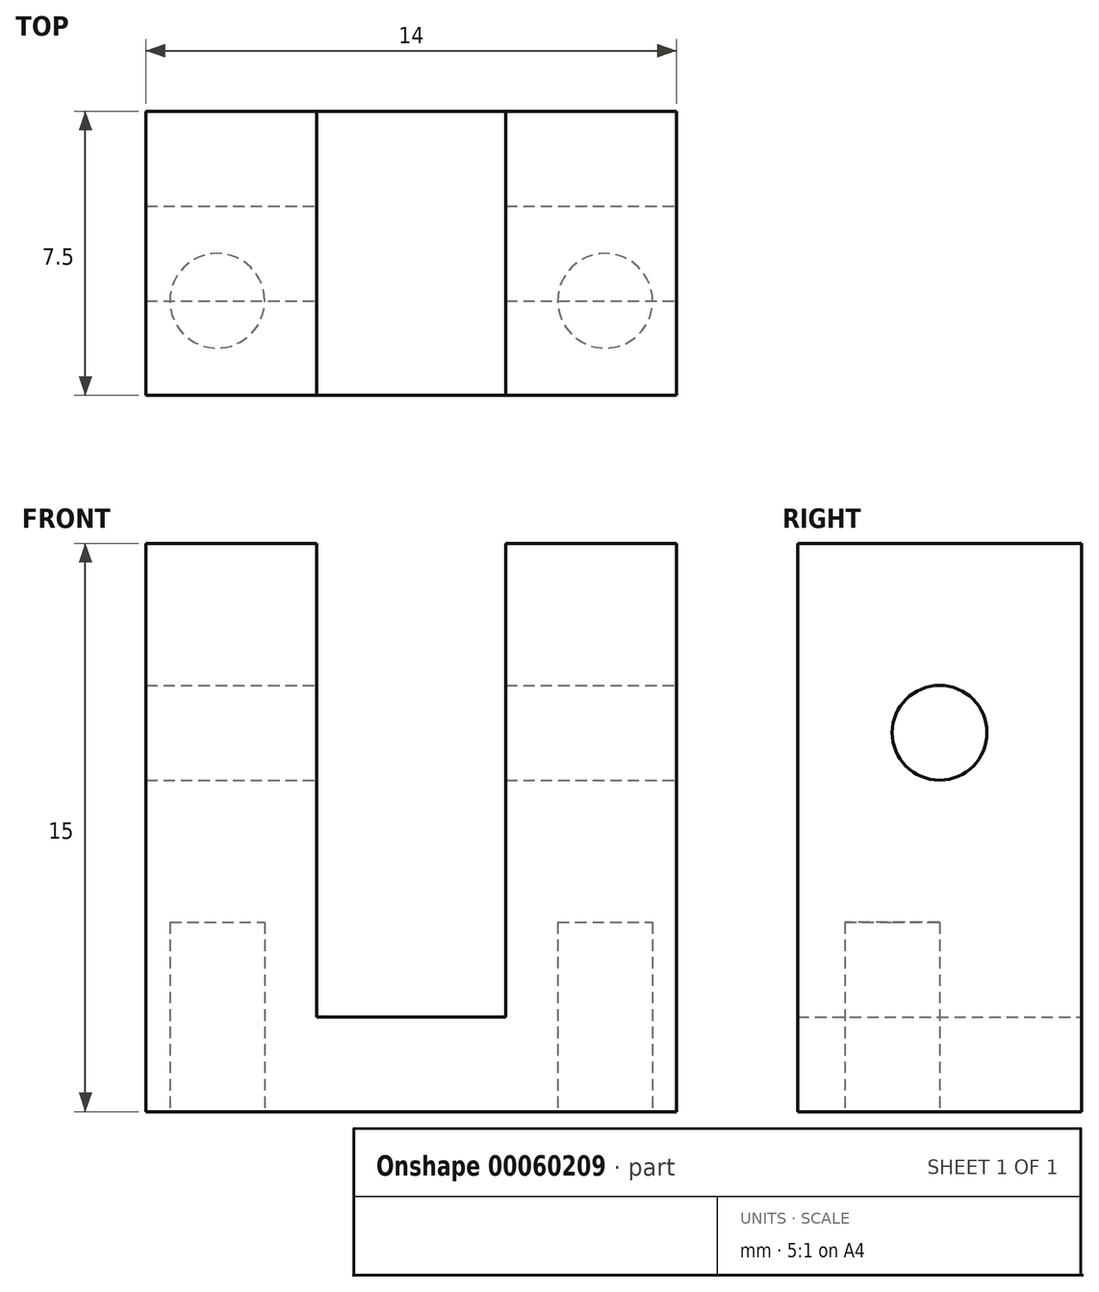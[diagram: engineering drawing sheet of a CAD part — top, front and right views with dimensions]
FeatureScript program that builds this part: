
annotation { "Feature Type Name" : "Feature", "Feature Type Description" : "" }
export const myFeature = defineFeature(function(context is Context, id is Id, definition is map)
    precondition{}
    {
        {
            var Q0;
            Q0=qCreatedBy(makeId("Front.planeOp"),FACE);
            var sketch = newSketch(context, id + "F0", { "sketchPlane" : qUnion([Q0])});
            skLineSegment(sketch, "E0", {"start": v(0, 0) * mm, "end": v(7, 0) * mm});
            skLineSegment(sketch, "E1", {"start": v(7, 0) * mm, "end": v(7, 15) * mm});
            skLineSegment(sketch, "E2", {"start": v(7, 15) * mm, "end": v(2.5, 15) * mm});
            skLineSegment(sketch, "E3", {"start": v(2.5, 15) * mm, "end": v(2.5, 2.5) * mm});
            skLineSegment(sketch, "E4", {"start": v(2.5, 2.5) * mm, "end": v(-2.5, 2.5) * mm});
            skLineSegment(sketch, "E5", {"start": v(-2.5, 2.5) * mm, "end": v(-2.5, 15) * mm});
            skLineSegment(sketch, "E6", {"start": v(-2.5, 15) * mm, "end": v(-7, 15) * mm});
            skLineSegment(sketch, "E7", {"start": v(-7, 15) * mm, "end": v(-7, 0) * mm});
            skLineSegment(sketch, "E8", {"start": v(-7, 0) * mm, "end": v(0, 0) * mm});
            skSolve(sketch);
        }
        {
            var Q0;
            Q0 = qSketchRegion(id + "F0", true);
            extrude(context, id + "F1", {"entities" : qUnion([Q0]), "endBound" : BoundingType.SYMMETRIC, "depth" : 7.5 * mm});
        }
        {
            var Q0;
            Q0=makeQuery(id+"F1.opExtrude","SWEPT_FACE",FACE,{"disambiguationData":[OSD([sQuery(id+"F0.wireOp",EDGE,"E1")])]});
            var sketch = newSketch(context, id + "F2", { "sketchPlane" : qUnion([Q0])});
            skCircle(sketch, "E9", {"center": v(0, 10) * mm, "radius": 1.25 * mm});
            skSolve(sketch);
        }
        {
            var Q0;
            Q0 = qSketchRegion(id + "F2", true);
            extrude(context, id + "F3", {"entities" : qUnion([Q0]), "operationType" : NewBodyOperationType.REMOVE, "oppositeDirection" : true, "depth" : 25 * mm});
        }
        {
            var Q0;
            Q0=makeQuery(id+"F1.opExtrude","SWEPT_FACE",FACE,{"disambiguationData":[OSD([sQuery(id+"F0.wireOp",EDGE,"E0"),sQuery(id+"F0.wireOp",EDGE,"E8")])]});
            var sketch = newSketch(context, id + "F4", { "sketchPlane" : qUnion([Q0])});
            skCircle(sketch, "E10", {"center": v(5.12, 1.25) * mm, "radius": 1.25 * mm});
            skCircle(sketch, "E11", {"center": v(-5.12, 1.25) * mm, "radius": 1.25 * mm});
            skSolve(sketch);
        }
        {
            var Q0;
            Q0 = qSketchRegion(id + "F4", true);
            extrude(context, id + "F5", {"entities" : qUnion([Q0]), "operationType" : NewBodyOperationType.REMOVE, "oppositeDirection" : true, "depth" : 5 * mm});
        }
    });
